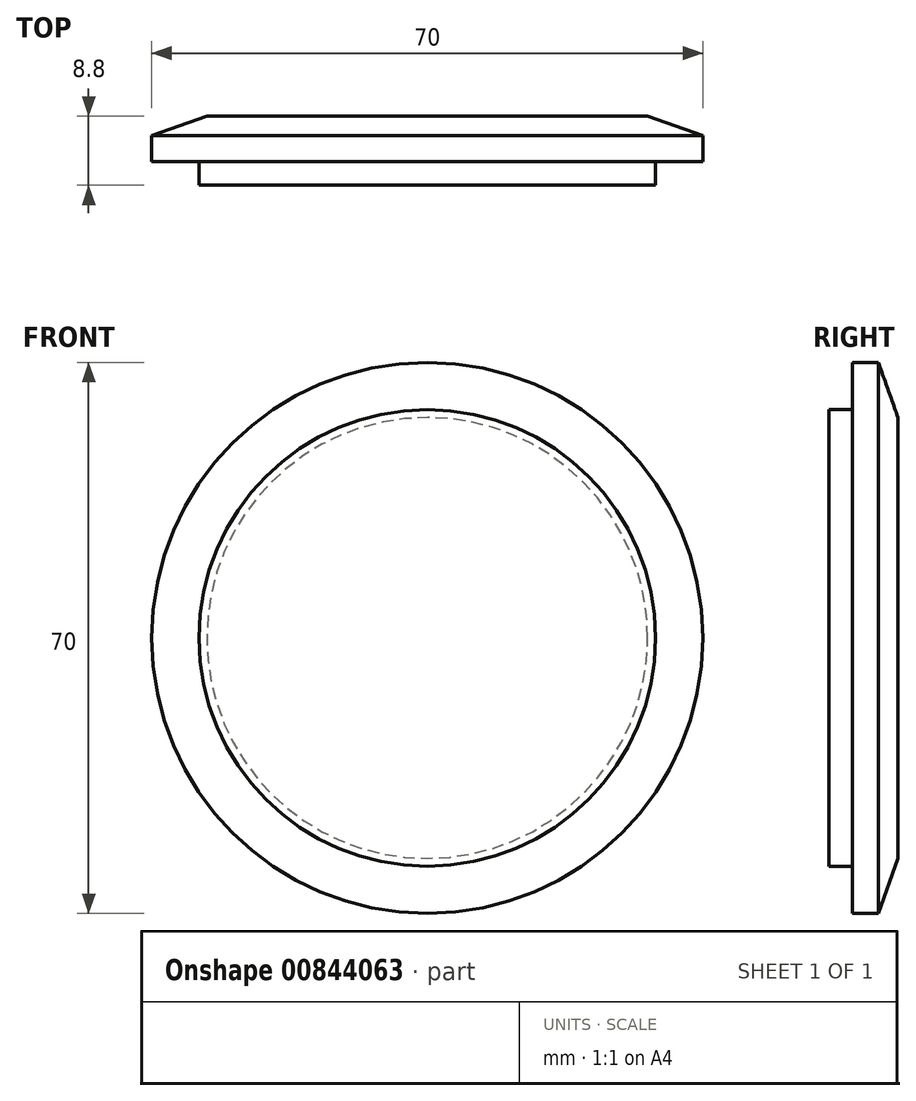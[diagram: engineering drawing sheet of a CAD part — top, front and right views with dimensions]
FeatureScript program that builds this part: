
annotation { "Feature Type Name" : "Feature", "Feature Type Description" : "" }
export const myFeature = defineFeature(function(context is Context, id is Id, definition is map)
    precondition{}
    {
        {
            var Q0;
            Q0=qCreatedBy(makeId("Right.planeOp"), FACE);
            var sketch = newSketch(context, id + "F0", { "sketchPlane" : qUnion([Q0])});
            skLineSegment(sketch, "E0", {"start": v(0, 35) * mm, "end": v(3.3, 35) * mm});
            skLineSegment(sketch, "E1", {"start": v(3.3, 35) * mm, "end": v(5.8, 28) * mm});
            skLineSegment(sketch, "E2", {"start": v(5.8, 28) * mm, "end": v(5.8, 0) * mm});
            skLineSegment(sketch, "E3", {"start": v(5.8, 0) * mm, "end": v(-3, 0) * mm});
            skLineSegment(sketch, "E4", {"start": v(-3, 0) * mm, "end": v(-3, 29) * mm});
            skLineSegment(sketch, "E5", {"start": v(-3, 29) * mm, "end": v(0, 29) * mm});
            skLineSegment(sketch, "E6", {"start": v(0, 29) * mm, "end": v(0, 35) * mm});
            skLineSegment(sketch, "E7", {"start": v(18.47, 39.97) * mm, "end": v(19.63, 36.8) * mm, "construction": true});
            skLineSegment(sketch, "E8", {"start": v(0, 0) * mm, "end": v(82.54, 0) * mm, "construction": true});
            skSolve(sketch);
        }
        {
            var Q0;
            Q0 = qSketchRegion(id + "F0", true);
            var Q1;
            Q1=sQuery(id+"F0.wireOp",EDGE,"E3");
            revolve(context, id + "F1", {"surfaceOperationType" : NewSurfaceOperationType.NEW, "entities" : qUnion([Q0]), "axis" : qUnion([Q1]), "revolveType" : RevolveType.FULL});
        }
    });
